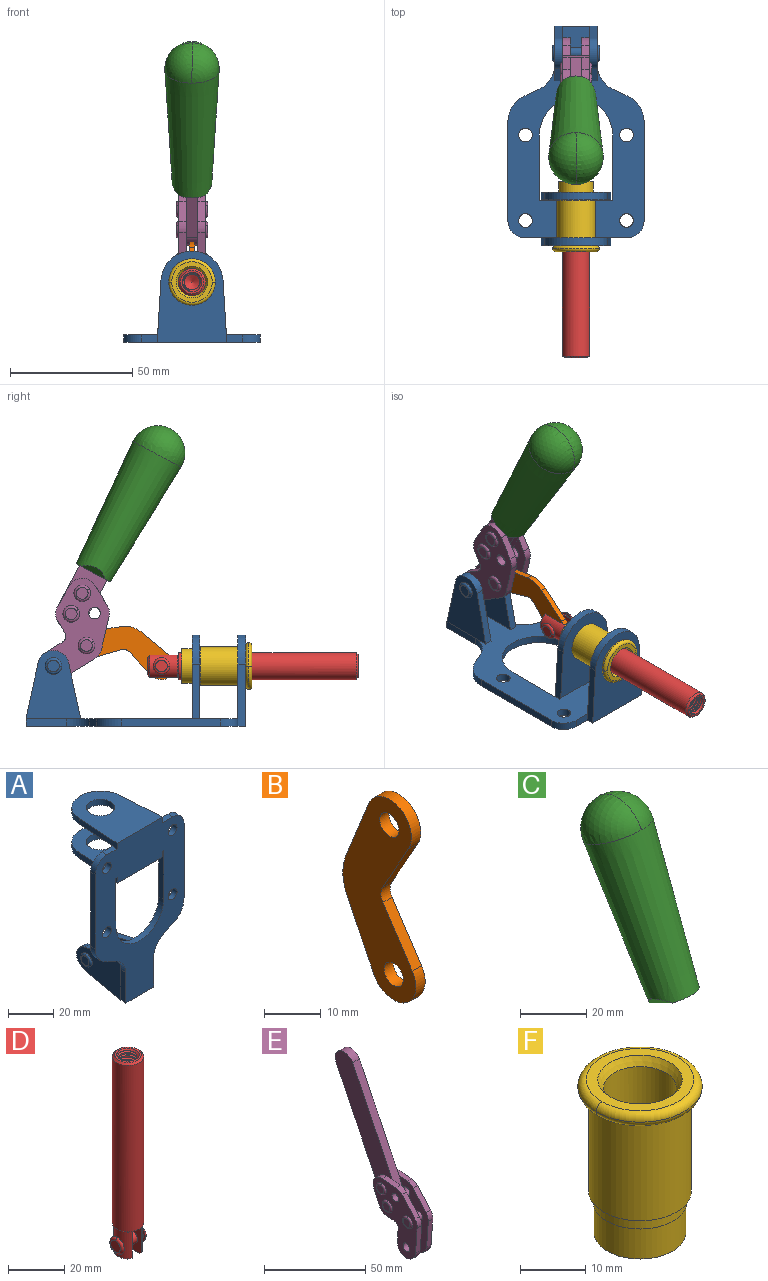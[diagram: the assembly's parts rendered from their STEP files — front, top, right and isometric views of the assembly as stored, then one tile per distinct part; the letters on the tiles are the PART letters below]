
ASSEMBLY  parts=6 mates=6
PART A: 55 faces, bbox 55.7x37.4x89.8 mm
  f0: torus R=2.41mm, axis (-1,0,0), area 15mm2, adj f11,f15,f25
  f1: torus R=2.41mm, axis (-1,0,0), area 15mm2, adj f10,f12,f22
  f2: cylinder r=2.78mm len=5.56mm, axis (0,-1,0), area 54.2mm2, adj f30,f54
  f3: cylinder r=14.99mm len=29.97mm, axis (0,-1,0), area 145.9mm2, adj f30,f49,f53,f54
  f4: cylinder r=2.78mm len=5.56mm, axis (0,-1,0), area 54.2mm2, adj f30,f54
  f5: cylinder r=2.78mm len=5.56mm, axis (0,-1,0), area 54.2mm2, adj f30,f54
  f6: cylinder r=2.78mm len=5.56mm, axis (0,-1,0), area 54.2mm2, adj f30,f54
  f7: cylinder r=6.35mm len=12.7mm, axis (0,0,1), area 123.6mm2, adj f27,f51
  f8: cylinder r=6.35mm len=12.7mm, axis (0,0,-1), area 124.7mm2, adj f21,f35
  f9: cylinder r=2.41mm len=11.18mm, axis (-1,0,0), area 169.4mm2, adj f16,f19
  f10: plane 4.83x4.83mm, normal (1,0,0), area 18.3mm2, adj f1,f12
  f11: plane 4.83x4.83mm, normal (-1,0,0), area 18.3mm2, adj f0,f15
  f12: torus R=2.41mm, axis (-1,0,0), area 15mm2, adj f1,f10,f22
  f13: cylinder r=6.35mm len=12.41mm, axis (1,0,0), area 53.4mm2, adj f18,f19,f22,f23
  f14: cylinder r=6.35mm len=12.41mm, axis (-1,0,0), area 53.4mm2, adj f16,f17,f24,f25
  f15: torus R=2.41mm, axis (-1,0,0), area 15mm2, adj f0,f11,f25
  f16: plane 27.86x22.35mm, normal (1,0,0), area 425.4mm2, adj f9,f14,f17,f24,f30
  f17: plane 22.86x4.97mm, normal (0,0.21,0.98), area 72.5mm2, adj f14,f16,f25,f30
  f18: plane 22.86x4.97mm, normal (0,0.21,0.98), area 72.5mm2, adj f13,f19,f22,f30
  f19: plane 27.86x22.35mm, normal (-1,0,0), area 425.4mm2, adj f9,f13,f18,f23,f30
  f20: cylinder r=12.7mm len=25.35mm, axis (0,0,-1), area 119.8mm2, adj f21,f34,f35,f36
  f21: plane 34.21x28.07mm, normal (0,0,-1), area 702.4mm2, adj f8,f20,f30,f34,f36
  f22: plane 27.96x22.45mm, normal (1,0,0), area 407.2mm2, adj f1,f12,f13,f18,f23,f30,f42,f43
  f23: plane 22.86x4.97mm, normal (0,0.21,-0.98), area 72.5mm2, adj f13,f19,f22,f44
  f24: plane 22.86x4.97mm, normal (0,0.21,-0.98), area 72.5mm2, adj f14,f16,f25,f44
  f25: plane 27.86x22.35mm, normal (-1,0,0), area 407.1mm2, adj f0,f14,f15,f17,f24,f30,f45,f46
  f26: plane 3.1x0.95mm, normal (0,0,-1), area 2.7mm2, adj f30,f49,f50,f54
  f27: plane 34.21x28.07mm, normal (0,0,1), area 702.4mm2, adj f7,f28,f30,f50,f52
  f28: cylinder r=12.7mm len=25.35mm, axis (0,0,1), area 118.8mm2, adj f27,f50,f51,f52
  f29: plane 3.1x0.95mm, normal (0,0,-1), area 2.7mm2, adj f30,f52,f53,f54
  f30: plane 86.54x55.63mm, normal (0,1,0), area 2362.9mm2, adj f2,f3,f4,f5,f6,f16,f17,f18
  f31: plane 40.56x3.1mm, normal (-1,0,0), area 125.7mm2, adj f30,f32,f48,f54
  f32: cylinder r=7.11mm len=7.11mm, axis (0,-1,0), area 34.6mm2, adj f30,f31,f33,f54
  f33: plane 6.67x3.1mm, normal (0,0,1), area 20.4mm2, adj f30,f32,f34,f54
  f34: plane 25.39x3.13mm, normal (-1,0.06,0), area 79.5mm2, adj f20,f21,f33,f35,f54
  f35: plane 37.31x28.45mm, normal (0,0,1), area 789.9mm2, adj f8,f20,f34,f36,f54
  f36: plane 25.39x3.13mm, normal (1,0.06,0), area 79.5mm2, adj f20,f21,f35,f37,f54
  f37: plane 6.67x3.1mm, normal (0,0,1), area 20.4mm2, adj f30,f36,f38,f54
  f38: cylinder r=7.11mm len=7.11mm, axis (0,-1,0), area 34.6mm2, adj f30,f37,f39,f54
  f39: plane 40.56x3.1mm, normal (1,0,0), area 125.7mm2, adj f30,f38,f40,f54
  f40: cylinder r=11.18mm len=10.16mm, axis (0,-1,0), area 39.5mm2, adj f30,f39,f41,f54
  f41: plane 6.09x3.1mm, normal (0.42,0,-0.91), area 20.8mm2, adj f30,f40,f42,f54
  f42: cylinder r=11.18mm len=9.41mm, axis (0,-1,0), area 37.2mm2, adj f22,f30,f41,f43,f54
  f43: plane 16.5x3.1mm, normal (1,0,0), area 51.1mm2, adj f22,f42,f44,f54
  f44: plane 17.37x3.1mm, normal (0,0,-1), area 53.8mm2, adj f23,f24,f30,f43,f45,f54
  f45: plane 16.5x3.1mm, normal (-1,0,0), area 51.1mm2, adj f25,f44,f46,f54
  f46: cylinder r=11.18mm len=9.41mm, axis (0,-1,0), area 37.2mm2, adj f25,f30,f45,f47,f54
  f47: plane 6.09x3.1mm, normal (-0.42,0,-0.91), area 20.8mm2, adj f30,f46,f48,f54
  f48: cylinder r=11.18mm len=10.16mm, axis (0,-1,0), area 39.5mm2, adj f30,f31,f47,f54
  f49: plane 26.54x3.1mm, normal (-1,0,0), area 82.3mm2, adj f3,f26,f30,f54
  f50: plane 25.39x3.1mm, normal (1,0.06,0), area 78.8mm2, adj f26,f27,f28,f51,f54
  f51: plane 37.31x28.45mm, normal (0,0,-1), area 789.9mm2, adj f7,f28,f50,f52,f54
  f52: plane 25.39x3.1mm, normal (-1,0.06,0), area 78.8mm2, adj f27,f28,f29,f51,f54
  f53: plane 26.54x3.1mm, normal (1,0,0), area 82.3mm2, adj f3,f29,f30,f54
  f54: plane 89.66x55.63mm, normal (0,-1,0), area 2678.5mm2, adj f2,f3,f4,f5,f6,f26,f29,f31
PART B: 12 faces, bbox 2.3x18.2x42.8 mm
  f0: cylinder r=2.4mm len=4.8mm, axis (1,0,0), area 34.9mm2, adj f4,f11
  f1: cylinder r=10.41mm len=8.47mm, axis (1,0,0), area 20.2mm2, adj f4,f9,f10,f11
  f2: cylinder r=3.05mm len=3.16mm, axis (1,0,0), area 7.7mm2, adj f4,f6,f7,f11
  f3: cylinder r=2.4mm len=4.8mm, axis (1,0,0), area 34.9mm2, adj f4,f11
  f4: plane 42.81x18.23mm, normal (-1,0,0), area 414.1mm2, adj f0,f1,f2,f3,f5,f6,f7,f8
  f5: cylinder r=5.54mm len=10.67mm, axis (1,0,0), area 41.8mm2, adj f4,f6,f10,f11
  f6: plane 11.66x6.53mm, normal (0,-0.87,-0.49), area 30.9mm2, adj f2,f4,f5,f11
  f7: plane 11.17x7.33mm, normal (0,-0.84,0.55), area 30.9mm2, adj f2,f4,f8,f11
  f8: cylinder r=5.54mm len=10.51mm, axis (1,0,0), area 41.8mm2, adj f4,f7,f9,f11
  f9: plane 13.67x6.67mm, normal (0,0.9,-0.44), area 35.1mm2, adj f1,f4,f8,f11
  f10: plane 14.1x5.7mm, normal (0,0.93,0.37), area 35.1mm2, adj f1,f4,f5,f11
  f11: plane 42.81x18.23mm, normal (1,0,0), area 414.1mm2, adj f0,f1,f2,f3,f5,f6,f7,f8
PART C: 11 faces, bbox 22.3x42.6x64.5 mm
  f0: sphere r=11.13mm, area 411.4mm2, adj f1,f8
  f1: cone r=11.11mm half-angle=3.3deg, axis (0,0.44,0.9), area 3251.8mm2, adj f0,f7,f8,f9,f10
  f2: cylinder r=6.16mm len=11.7mm, axis (1,0,0), area 89.5mm2, adj f3,f4,f5,f6
  f3: plane 60.23x36.75mm, normal (-1,0,0), area 763.6mm2, adj f2,f4,f6,f10
  f4: plane 51.37x25.05mm, normal (0,0.9,-0.44), area 264.2mm2, adj f2,f3,f5,f10
  f5: plane 60.23x36.75mm, normal (1,0,0), area 763.6mm2, adj f2,f4,f6,f10
  f6: plane 51.37x25.05mm, normal (0,-0.9,0.44), area 264.2mm2, adj f2,f3,f5,f10
  f7: plane 9.95x5.95mm, normal (0.71,-0.31,-0.64), area 25.8mm2, adj f1,f10
  f8: sphere r=11.13mm, area 411.4mm2, adj f0,f1
  f9: plane 9.95x5.95mm, normal (-0.71,-0.31,-0.64), area 25.8mm2, adj f1,f10
  f10: plane 14.27x11.38mm, normal (0,-0.44,-0.9), area 106.7mm2, adj f1,f3,f4,f5,f6,f7,f9
PART D: 48 faces, bbox 12.6x11.1x86.1 mm
  f0: torus R=2.41mm, axis (-1,0,0), area 15mm2, adj f30,f32,f34
  f1: torus R=2.41mm, axis (-1,0,0), area 15mm2, adj f29,f31,f33
  f2: cylinder r=5.54mm len=72.39mm, axis (0,0,1), area 2518.5mm2, adj f3,f4,f42,f43
  f3: cone r=5.54mm half-angle=45deg, axis (0,0,1), area 7.6mm2, adj f2,f5,f41
  f4: cone r=5.54mm half-angle=45deg, axis (0,0,-1), area 34.9mm2, adj f2,f39
  f5: cylinder r=5.08mm len=11.48mm, axis (0,0,1), area 108.3mm2, adj f3,f7,f8,f41
  f6: cylinder r=2.41mm len=4.83mm, axis (-1,0,0), area 71.2mm2, adj f40,f41
  f7: cylinder r=2.41mm len=4.83mm, axis (-1,0,0), area 7.6mm2, adj f5,f34
  f8: cone r=5.08mm half-angle=45deg, axis (0,0,1), area 10.6mm2, adj f5,f37,f41
  f9: cone r=3.98mm half-angle=45deg, axis (0,0,1), area 17.6mm2, adj f27,f39,f45,f46,f47
  f10: cylinder r=2.41mm len=4.83mm, axis (-1,0,0), area 7.6mm2, adj f33,f38
  f11: cylinder r=3.2mm len=6.4mm, axis (0,0,1), area 78.4mm2, adj f12,f28,f44,f45,f47
  f12: cylinder r=3.2mm len=6.4mm, axis (0,0,1), area 10.5mm2, adj f11,f13,f45,f47
  f13: cylinder r=3.2mm len=6.4mm, axis (0,0,1), area 10.5mm2, adj f12,f14,f45,f47
  f14: cylinder r=3.2mm len=6.4mm, axis (0,0,1), area 10.5mm2, adj f13,f15,f45,f47
  f15: cylinder r=3.2mm len=6.4mm, axis (0,0,1), area 10.5mm2, adj f14,f16,f45,f47
  f16: cylinder r=3.2mm len=6.4mm, axis (0,0,1), area 10.5mm2, adj f15,f17,f45,f47
  f17: cylinder r=3.2mm len=6.4mm, axis (0,0,1), area 10.5mm2, adj f16,f18,f45,f47
  f18: cylinder r=3.2mm len=6.4mm, axis (0,0,1), area 10.5mm2, adj f17,f19,f45,f47
  f19: cylinder r=3.2mm len=6.4mm, axis (0,0,1), area 10.5mm2, adj f18,f20,f45,f47
  f20: cylinder r=3.2mm len=6.4mm, axis (0,0,1), area 10.5mm2, adj f19,f21,f45,f47
  f21: cylinder r=3.2mm len=6.4mm, axis (0,0,1), area 10.5mm2, adj f20,f22,f45,f47
  f22: cylinder r=3.2mm len=6.4mm, axis (0,0,1), area 10.5mm2, adj f21,f23,f45,f47
  f23: cylinder r=3.2mm len=6.4mm, axis (0,0,1), area 10.5mm2, adj f22,f24,f45,f47
  f24: cylinder r=3.2mm len=6.4mm, axis (0,0,1), area 10.5mm2, adj f23,f25,f45,f47
  f25: cylinder r=3.2mm len=6.4mm, axis (0,0,1), area 10.5mm2, adj f24,f26,f45,f47
  f26: cylinder r=3.2mm len=6.4mm, axis (0,0,1), area 10.5mm2, adj f25,f27,f45,f47
  f27: cylinder r=3.2mm len=6.4mm, axis (0,0,1), area 7.4mm2, adj f9,f26,f45,f47
  f28: cone r=3.2mm half-angle=60deg, axis (0,0,1), area 37.2mm2, adj f11
  f29: plane 4.83x4.83mm, normal (-1,0,0), area 18.3mm2, adj f1,f31
  f30: plane 4.83x4.83mm, normal (1,0,0), area 18.3mm2, adj f0,f32
  f31: torus R=2.41mm, axis (-1,0,0), area 15mm2, adj f1,f29,f33
  f32: torus R=2.41mm, axis (-1,0,0), area 15mm2, adj f0,f30,f34
  f33: plane 6.83x6.83mm, normal (1,0,0), area 18.3mm2, adj f1,f10,f31
  f34: plane 6.83x6.83mm, normal (-1,0,0), area 18.3mm2, adj f0,f7,f32
  f35: cone r=5.08mm half-angle=45deg, axis (0,0,1), area 10.6mm2, adj f36,f38,f40
  f36: plane 7.25x1.97mm, normal (0,0,-1), area 10mm2, adj f35,f40
  f37: plane 7.25x1.97mm, normal (0,0,-1), area 10mm2, adj f8,f41
  f38: cylinder r=5.08mm len=11.48mm, axis (0,0,1), area 108.3mm2, adj f10,f35,f40,f42
  f39: plane 9.55x9.55mm, normal (0,0,1), area 22mm2, adj f4,f9
  f40: plane 12.76x10.09mm, normal (1,0,0), area 95.7mm2, adj f6,f35,f36,f38,f42,f43
  f41: plane 12.76x10.09mm, normal (-1,0,0), area 95.7mm2, adj f3,f5,f6,f8,f37,f43
  f42: cone r=5.54mm half-angle=45deg, axis (0,0,1), area 7.6mm2, adj f2,f38,f40
  f43: plane 11.07x4.7mm, normal (0,0,-1), area 50.4mm2, adj f2,f40,f41
  f44: plane 0.89x0.62mm, normal (-1,0,0), area 0.3mm2, adj f11,f45,f46,f47
  f45: bspline ~24.8x7.63mm, area 266.6mm2, adj f9,f11,f12,f13,f14,f15,f16,f17
  f46: bspline ~24.87x7.63mm, area 73.6mm2, adj f9,f44,f45,f47
  f47: bspline ~24.98x7.63mm, area 272.5mm2, adj f9,f11,f12,f13,f14,f15,f16,f17
PART E: 59 faces, bbox 12.9x60.2x99.6 mm
  f0: torus R=2.39mm, axis (-1,0,0), area 14.9mm2, adj f20,f43,f51
  f1: torus R=2.39mm, axis (-1,0,0), area 14.9mm2, adj f19,f42,f51
  f2: torus R=2.39mm, axis (-1,0,0), area 14.9mm2, adj f18,f35,f51
  f3: torus R=2.39mm, axis (-1,0,0), area 14.9mm2, adj f14,f17,f23
  f4: torus R=2.39mm, axis (-1,0,0), area 14.9mm2, adj f13,f16,f23
  f5: torus R=2.39mm, axis (-1,0,0), area 14.9mm2, adj f12,f15,f23
  f6: cylinder r=2.39mm len=4.78mm, axis (1,0,0), area 46.5mm2, adj f48,f50,f51
  f7: cylinder r=2.39mm len=4.78mm, axis (1,0,0), area 46.5mm2, adj f50,f51
  f8: cylinder r=6.35mm len=12.68mm, axis (1,0,0), area 61.8mm2, adj f38,f39,f50,f51
  f9: cylinder r=2.39mm len=4.78mm, axis (-1,0,0), area 70.5mm2, adj f46,f50
  f10: cylinder r=2.39mm len=4.78mm, axis (-1,0,0), area 46.5mm2, adj f23,f45,f46
  f11: cylinder r=2.39mm len=4.78mm, axis (-1,0,0), area 46.5mm2, adj f23,f46
  f12: plane 4.78x4.78mm, normal (1,0,0), area 17.9mm2, adj f5,f15
  f13: plane 4.78x4.78mm, normal (1,0,0), area 17.9mm2, adj f4,f16
  f14: plane 4.78x4.78mm, normal (1,0,0), area 17.9mm2, adj f3,f17
  f15: torus R=2.39mm, axis (-1,0,0), area 14.9mm2, adj f5,f12,f23
  f16: torus R=2.39mm, axis (-1,0,0), area 14.9mm2, adj f4,f13,f23
  f17: torus R=2.39mm, axis (-1,0,0), area 14.9mm2, adj f3,f14,f23
  f18: plane 4.78x4.78mm, normal (-1,0,0), area 17.9mm2, adj f2,f35
  f19: plane 4.78x4.78mm, normal (-1,0,0), area 17.9mm2, adj f1,f42
  f20: plane 4.78x4.78mm, normal (-1,0,0), area 17.9mm2, adj f0,f43
  f21: plane 2.26x0.2mm, normal (1,0,0), area 0.2mm2, adj f31,f44
  f22: plane 2.26x0.2mm, normal (-1,0,0), area 0.2mm2, adj f41,f44
  f23: plane 39.37x30.77mm, normal (1,0,0), area 565.5mm2, adj f3,f4,f5,f10,f11,f15,f16,f17
  f24: cylinder r=6.1mm len=4.15mm, axis (-1,0,0), area 14.7mm2, adj f23,f25,f32,f46
  f25: plane 10.25x9.01mm, normal (0,-0.75,0.66), area 42.3mm2, adj f23,f24,f26,f46
  f26: cylinder r=6.35mm len=4.64mm, axis (-1,0,0), area 15.6mm2, adj f23,f25,f27,f46
  f27: plane 15.84x3.1mm, normal (0,-1,-0.07), area 49.2mm2, adj f23,f26,f28,f46
  f28: cylinder r=6.35mm len=12.68mm, axis (-1,0,0), area 61.8mm2, adj f23,f27,f29,f46
  f29: plane 8.11x3.1mm, normal (0,1,0.07), area 25.2mm2, adj f23,f28,f30,f46
  f30: cylinder r=3.05mm len=3.25mm, axis (-1,0,0), area 14.8mm2, adj f23,f29,f31,f46
  f31: plane 5.99x3.1mm, normal (0,0.07,-1), area 18.6mm2, adj f21,f23,f30,f44,f46
  f32: plane 9.5x3.1mm, normal (0,-0.07,1), area 29.5mm2, adj f23,f24,f33,f46,f47
  f33: cylinder r=6.1mm len=8.63mm, axis (-1,0,0), area 39.1mm2, adj f23,f32,f34,f47
  f34: plane 8.65x3.96mm, normal (0,0.91,-0.42), area 29.5mm2, adj f23,f33,f44,f47
  f35: torus R=2.39mm, axis (-1,0,0), area 14.9mm2, adj f2,f18,f51
  f36: plane 10.25x9.01mm, normal (0,-0.75,0.66), area 42.3mm2, adj f37,f49,f50,f51
  f37: cylinder r=6.35mm len=4.64mm, axis (1,0,0), area 15.6mm2, adj f36,f38,f50,f51
  f38: plane 15.84x3.1mm, normal (0,-1,-0.07), area 49.2mm2, adj f8,f37,f50,f51
  f39: plane 8.11x3.1mm, normal (0,1,0.07), area 25.2mm2, adj f8,f40,f50,f51
  f40: cylinder r=3.05mm len=3.25mm, axis (1,0,0), area 14.8mm2, adj f39,f41,f50,f51
  f41: plane 5.99x3.1mm, normal (0,0.07,-1), area 18.6mm2, adj f22,f40,f44,f50,f51
  f42: torus R=2.39mm, axis (-1,0,0), area 14.9mm2, adj f1,f19,f51
  f43: torus R=2.39mm, axis (-1,0,0), area 14.9mm2, adj f0,f20,f51
  f44: cylinder r=6.35mm len=12.12mm, axis (-1,0,0), area 128.9mm2, adj f21,f22,f23,f31,f34,f41,f46,f47
  f45: plane 2.65x1.35mm, normal (1,0,0), area 1mm2, adj f10,f55
  f46: plane 39.08x20.42mm, normal (-1,0,0), area 412.5mm2, adj f9,f10,f11,f24,f25,f26,f27,f28
  f47: plane 77.62x39.82mm, normal (1,0,0), area 850mm2, adj f32,f33,f34,f44,f53,f54,f55
  f48: plane 2.65x1.35mm, normal (-1,0,0), area 1mm2, adj f6,f55
  f49: cylinder r=6.1mm len=4.15mm, axis (1,0,0), area 14.7mm2, adj f36,f50,f51,f56
  f50: plane 39.08x20.42mm, normal (1,0,0), area 412.5mm2, adj f6,f7,f8,f9,f36,f37,f38,f39
  f51: plane 39.37x30.77mm, normal (-1,0,0), area 565.5mm2, adj f0,f1,f2,f6,f7,f8,f35,f36
  f52: plane 8.65x3.96mm, normal (0,0.91,-0.42), area 29.5mm2, adj f44,f51,f57,f58
  f53: plane 68.49x33.4mm, normal (0,0.9,-0.44), area 358.1mm2, adj f44,f47,f54,f58
  f54: cylinder r=6.35mm len=12.06mm, axis (1,0,0), area 93.7mm2, adj f47,f53,f55,f58
  f55: plane 68.49x33.4mm, normal (0,-0.9,0.44), area 358.1mm2, adj f44,f45,f46,f47,f48,f50,f54,f58
  f56: plane 9.5x3.1mm, normal (0,-0.07,1), area 29.5mm2, adj f49,f50,f51,f57,f58
  f57: cylinder r=6.1mm len=8.63mm, axis (1,0,0), area 39.1mm2, adj f51,f52,f56,f58
  f58: plane 77.62x39.82mm, normal (-1,0,0), area 850mm2, adj f44,f52,f53,f54,f55,f56,f57
PART F: 15 faces, bbox 20.6x20.6x28.7 mm
  f0: torus R=8.26mm, axis (0,0,1), area 56.8mm2, adj f1,f10,f12
  f1: torus R=8.26mm, axis (0,0,1), area 56.8mm2, adj f0,f6,f13
  f2: cylinder r=5.59mm len=25.91mm, axis (0,0,1), area 909.6mm2, adj f3,f4
  f3: cone r=6.86mm half-angle=45deg, axis (0,0,-1), area 70.2mm2, adj f2,f14
  f4: cone r=6.47mm half-angle=30deg, axis (0,0,1), area 66.7mm2, adj f2,f13
  f5: cylinder r=7.04mm len=14.07mm, axis (0,0,1), area 252.6mm2, adj f11,f14
  f6: torus R=8.26mm, axis (0,0,1), area 56.8mm2, adj f1,f12,f13
  f7: cylinder r=7.16mm len=14.33mm, axis (0,0,1), area 91.5mm2, adj f9,f11
  f8: cylinder r=7.86mm len=18.42mm, axis (0,0,1), area 909.6mm2, adj f9,f10
  f9: plane 15.72x15.72mm, normal (0,0,-1), area 33mm2, adj f7,f8
  f10: plane 16.51x16.51mm, normal (0,0,-1), area 19.9mm2, adj f0,f8,f12
  f11: plane 14.33x14.33mm, normal (0,0,-1), area 5.7mm2, adj f5,f7
  f12: torus R=8.26mm, axis (0,0,1), area 56.8mm2, adj f0,f6,f10
  f13: plane 16.51x16.51mm, normal (0,0,1), area 82.7mm2, adj f1,f4,f6
  f14: plane 14.07x14.07mm, normal (0,0,-1), area 7.8mm2, adj f3,f5
PLACE A rot(axis=(1,0,0),90deg) t=(0,1.23,0)mm fixed
PLACE B rot(axis=(1,0,0),107.3deg) t=(0,11.28,5.7)mm
PLACE C rot(axis=(1,0,0),54.2deg) t=(0,-7.1,23.4)mm
PLACE D rot(axis=(1,0,0),90deg) t=(0,4.67,0)mm
PLACE E rot(axis=(1,0,0),54.2deg) t=(0,-7.1,23.4)mm
PLACE F rot(axis=(1,0,0),90deg) t=(0,1.23,0)mm
MATE revolute B.f3 <-> E.f4  axis (1,0,0) through (0,19.83,32.97)mm
MATE fastened E.f54 <-> C.f2  axis (1,0,0) through (0,-10.01,113.06)mm
MATE fastened A.f7 <-> F.f0  axis (0,-1,0) through (0,-45.16,24.61)mm
MATE slider A.f7 <-> D.f2  axis (0,-1,0) through (0,-45.16,24.61)mm
MATE revolute D.f6 <-> B.f5  axis (-1,0,0) through (0,-10.8,24.61)mm
MATE revolute E.f7 <-> A.f0  axis (-1,0,0) through (0,33.32,24.61)mm
